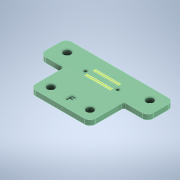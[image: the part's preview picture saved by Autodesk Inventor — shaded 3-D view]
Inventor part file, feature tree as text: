
AUTODESK INVENTOR PART (.ipt)
format: ipt  version: 2021 (Build 250183000, 183)  size: 566,784 bytes
history: native  units: mm
features: sketch x6, extrude x3, hole x2, emboss x1, projected_geometry x1
ambient origin geometry x8: Origin, YZ Plane, XZ Plane, XY Plane, X Axis, Y Axis, Z Axis, Center Point
bodies: Solid1 (feature_tree)
feature tree (13):
  extrude  "Extrusion1"  Depth=1.0mm
  hole  "Hole1"  [1 undecoded]
  hole  "Hole2"  [1 undecoded]
  sketch  "Sketch3"  dims[d6=2.3mm d7=0.0mm d8=27.5mm]
  extrude  "Extrusion2"  Depth=27.5mm
  extrude  "Extrusion3"  Depth=12.0mm
  emboss  "Emboss1"
  sketch  "Sketch1"  dims[d0=49.5mm d3=1.0mm]
  sketch  "Sketch2"  dims[d4=2.5mm d5=2.5mm]
  sketch  "Sketch4"  dims[d9=12.0mm d10=27.5mm]
  projected_geometry  "Projected Loop1"
  sketch  "Sketch5"  dims[d11=12.0mm d12=9.0mm]
  sketch  "Sketch6"  dims[d13=19.0mm d14=5.25mm d15=22.75mm d16=3.4mm d17=6.0mm d18=6.3mm d19=2.0mm d20=90.0deg d21=5.0mm d22=0.0mm d24=18.0mm d25=5.6mm d29=14.8mm d30=1.45mm d31=6.0mm d32=9.4mm d33=2.0mm d34=90.0deg d35=8.0mm d36=20.594885mm d41=1.5mm d42=2.8mm d45=7.4mm d47=14.3mm d48=14.3mm d49=7.86mm d50=1.5mm d51=90.0deg d52=0.55mm d53=70.0mm d55=0.8mm d56=10.0mm d58=10.0mm d60=70.0mm d62=0.8mm d63=10.0mm d65=10.0mm d67=20.0mm d69=3.8mm d70=10.0mm d72=10.0mm d74=1.15mm d75=1.15mm d76=0.01mm d77=0.0mm d79=70.0mm d81=10.0mm d83=70.0mm d85=10.0mm d87=20.0mm d89=10.0mm d91=70.0mm d93=10.0mm d95=70.0mm d97=10.0mm d99=20.0mm d101=10.0mm d102=0.8mm d103=0.8mm d104=0.5mm d106=14.8mm d107=7.15mm d108=1.1mm d109=1.1mm d110=80.0mm d112=0.8mm d113=20.0mm d115=4.5mm d118=80.0mm d120=0.8mm d121=20.0mm d123=4.5mm d126=0.005mm d127=0.0mm d129=2.5mm d130=2.5mm d131=2.6mm d132=0.0mm d133=7.4mm d134=1.5mm]
note: 2 required parameter values undecoded (feature->parameter linkage not recoverable at this tier; creation-order binding heuristic only, values carry confidence <= 0.55)
